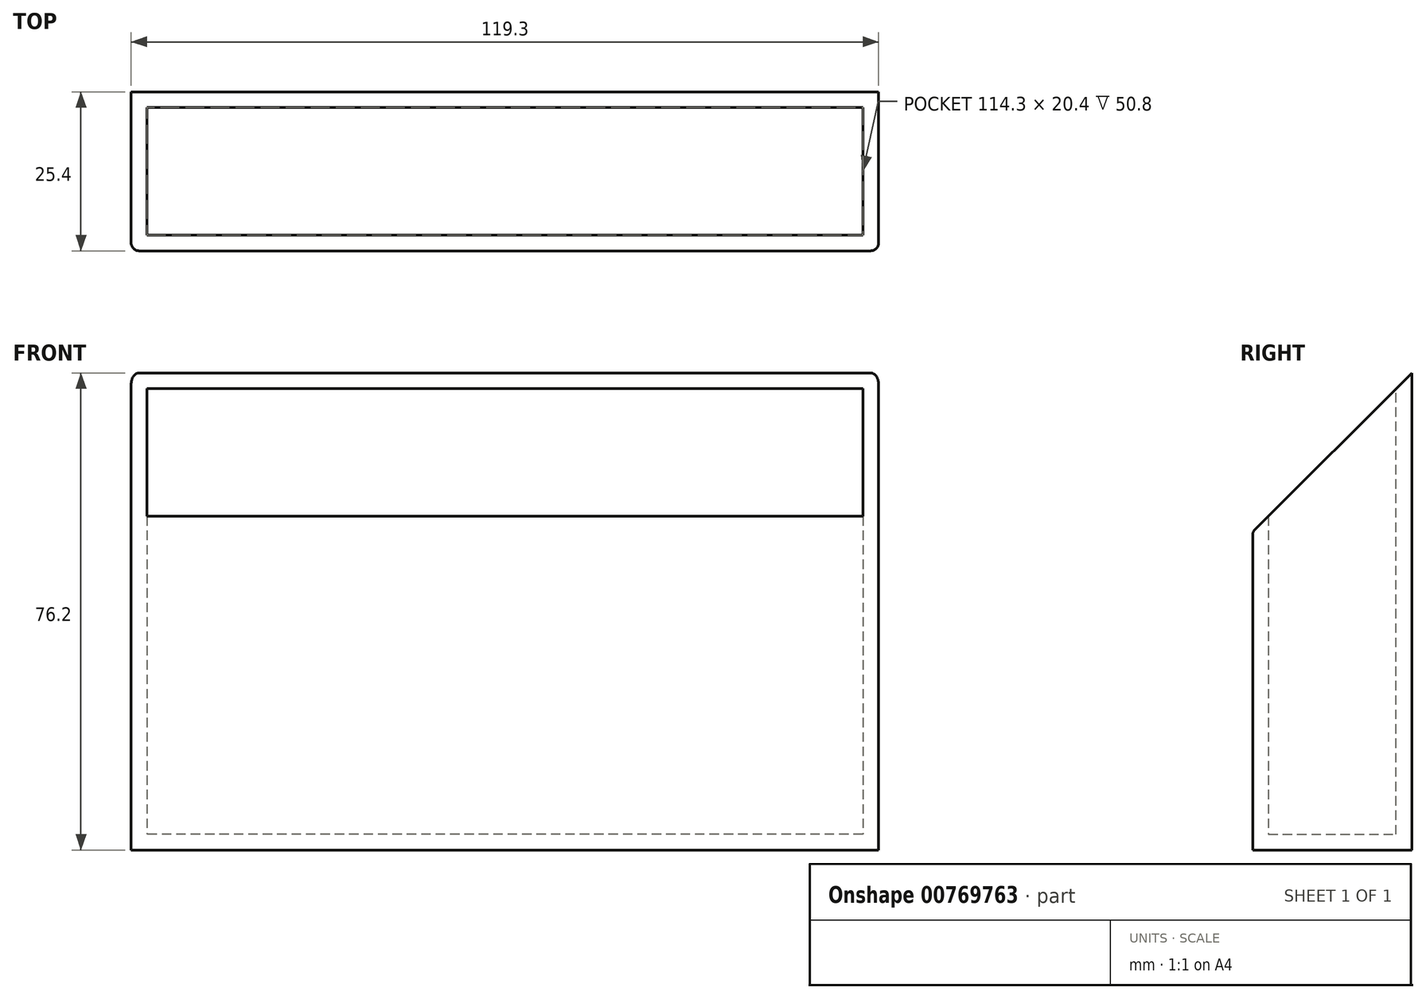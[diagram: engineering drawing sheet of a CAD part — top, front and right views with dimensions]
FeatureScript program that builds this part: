
annotation { "Feature Type Name" : "Feature", "Feature Type Description" : "" }
export const myFeature = defineFeature(function(context is Context, id is Id, definition is map)
    precondition{}
    {
        {
            var Q0;
            Q0=qCreatedBy(makeId("Right.planeOp"),FACE);
            var sketch = newSketch(context, id + "F0", { "sketchPlane" : qUnion([Q0])});
            skLineSegment(sketch, "E0", {"start": v(0, 0) * mm, "end": v(-25.4, 0) * mm});
            skLineSegment(sketch, "E1", {"start": v(-25.4, 0) * mm, "end": v(-25.4, 50.8) * mm});
            skLineSegment(sketch, "E2", {"start": v(-25.4, 50.8) * mm, "end": v(0, 76.2) * mm});
            skLineSegment(sketch, "E3", {"start": v(0, 76.2) * mm, "end": v(0, 0) * mm});
            skSolve(sketch);
        }
        {
            var Q0;
            Q0=makeQuery(id+"F0.imprint","IMPRINT",FACE,{"disambiguationData":[TD([[makeQuery(id+"F0.imprint","IMPRINT",EDGE,{"derivedFrom":sQuery(id+"F0.wireOp",EDGE,"E0")}),-1.0]])]});
            extrude(context, id + "F1", {"entities" : qUnion([Q0]), "endBound" : BoundingType.SYMMETRIC, "depth" : 114.3 * mm + 5 * mm, "offsetDistance" : 25 * mm});
        }
        {
            var Q0;
            Q0=qCreatedBy(makeId("Right.planeOp"),FACE);
            var sketch = newSketch(context, id + "F2", { "sketchPlane" : qUnion([Q0])});
            skLineSegment(sketch, "E4", {"start": v(-22.9, 53.3) * mm, "end": v(-22.9, 2.5) * mm});
            skLineSegment(sketch, "E5", {"start": v(-22.9, 2.5) * mm, "end": v(-2.5, 2.5) * mm});
            skLineSegment(sketch, "E6", {"start": v(-2.5, 2.5) * mm, "end": v(-2.5, 73.7) * mm});
            skLineSegment(sketch, "E7", {"start": v(-2.5, 73.7) * mm, "end": v(-22.9, 53.3) * mm});
            skSolve(sketch);
        }
        {
            var Q0;
            Q0 = qSketchRegion(id + "F2", true);
            extrude(context, id + "F3", {"entities" : qUnion([Q0]), "operationType" : NewBodyOperationType.REMOVE, "endBound" : BoundingType.SYMMETRIC, "depth" : 114.3 * mm, "offsetDistance" : 25 * mm});
        }
        {
            var Q0;
            Q0=makeQuery(id+"F1.opExtrude","CAP_EDGE",EDGE,{"disambiguationData":[OSD([sQuery(id+"F0.wireOp",EDGE,"E1")])],"isStart":true});
            var Q1;
            Q1=makeQuery(id+"F1.opExtrude","CAP_EDGE",EDGE,{"disambiguationData":[OSD([sQuery(id+"F0.wireOp",EDGE,"E1")])],"isStart":false});
            var Q2;
            Q2=makeQuery(id+"F1.opExtrude","CAP_EDGE",EDGE,{"disambiguationData":[OSD([sQuery(id+"F0.wireOp",EDGE,"E2")])],"isStart":false});
            var Q3;
            Q3=makeQuery(id+"F1.opExtrude","SWEPT_EDGE",EDGE,{"disambiguationData":[OSD([sQuery(id+"F0.wireOp",EDGE,"E1"),sQuery(id+"F0.wireOp",EDGE,"E2")])]});
            var Q4;
            Q4=makeQuery(id+"F1.opExtrude","CAP_EDGE",EDGE,{"disambiguationData":[OSD([sQuery(id+"F0.wireOp",EDGE,"E2")])],"isStart":true});
            var Q5;
            Q5=makeQuery(id+"F3.boolean.opBoolean","COPY",EDGE,{"derivedFrom":makeQuery(id+"F3.opExtrude","CAP_EDGE",EDGE,{"disambiguationData":[OSD([sQuery(id+"F2.wireOp",EDGE,"E7")])],"isStart":false})});
            var Q6;
            Q6=makeQuery(id+"F3.boolean.opBoolean","COPY",EDGE,{"derivedFrom":makeQuery(id+"F3.opExtrude","SWEPT_EDGE",EDGE,{"disambiguationData":[OSD([sQuery(id+"F2.wireOp",EDGE,"E4"),sQuery(id+"F2.wireOp",EDGE,"E7")])]})});
            var Q7;
            Q7=makeQuery(id+"F3.boolean.opBoolean","COPY",EDGE,{"derivedFrom":makeQuery(id+"F3.opExtrude","SWEPT_EDGE",EDGE,{"disambiguationData":[OSD([sQuery(id+"F2.wireOp",EDGE,"E6"),sQuery(id+"F2.wireOp",EDGE,"E7")])]})});
            var Q8;
            Q8=makeQuery(id+"F3.boolean.opBoolean","COPY",EDGE,{"derivedFrom":makeQuery(id+"F3.opExtrude","CAP_EDGE",EDGE,{"disambiguationData":[OSD([sQuery(id+"F2.wireOp",EDGE,"E7")])],"isStart":true})});
            fillet(context, id + "F4", {"entities" : qUnion([Q0, Q1, Q2, Q3, Q4, Q5, Q6, Q7, Q8]), "tangentPropagation" : true, "radius" : 1.25 * mm, "defaultsChanged" : false, "vertexSettings" : [], "allowEdgeOverflow" : false});
        }
    });
